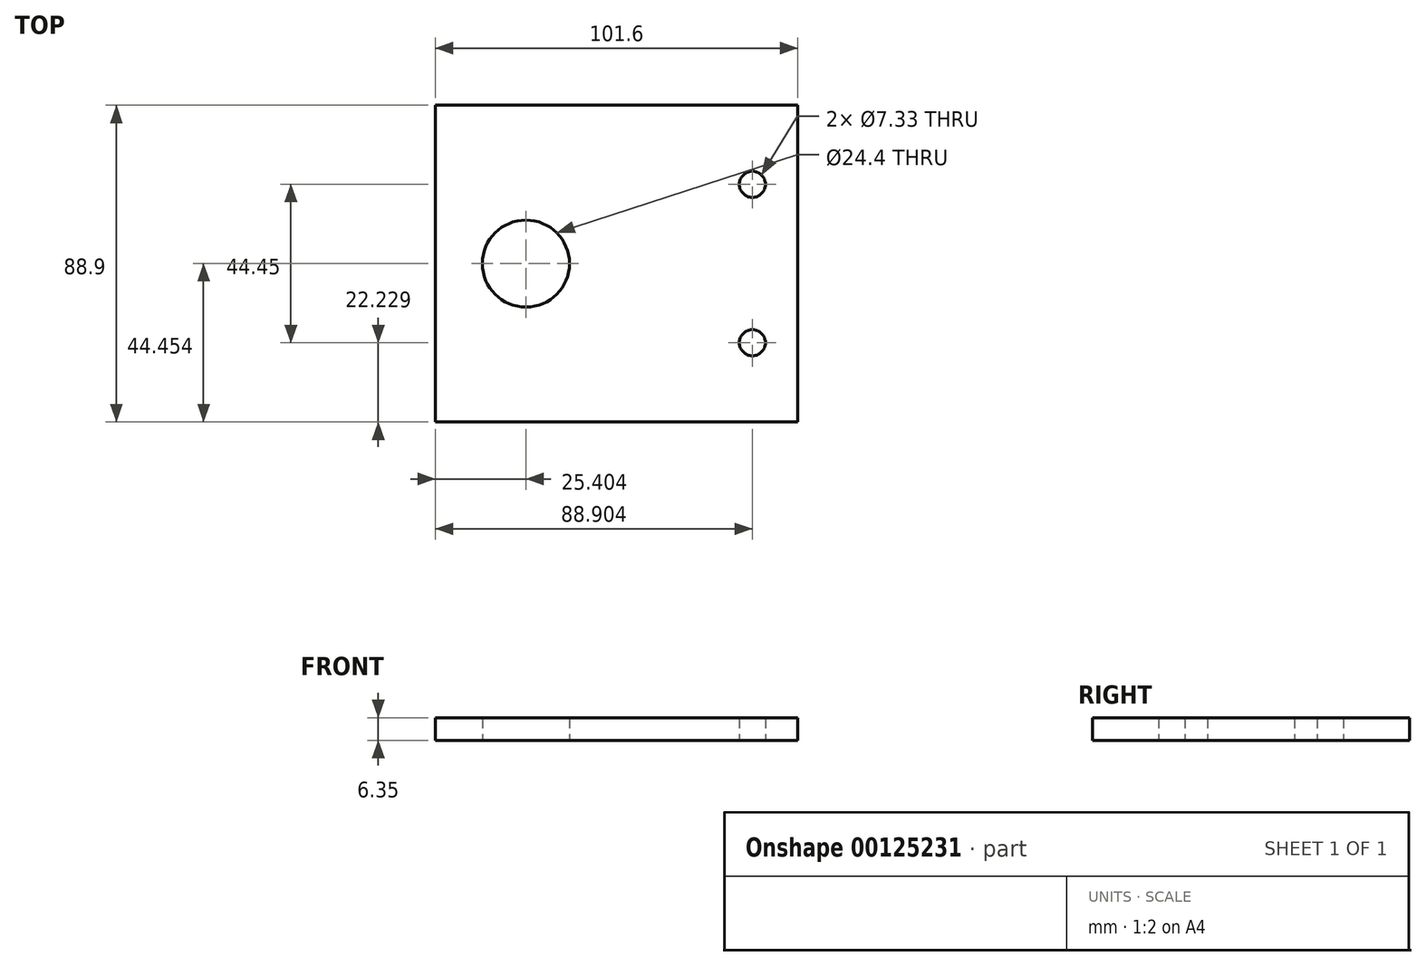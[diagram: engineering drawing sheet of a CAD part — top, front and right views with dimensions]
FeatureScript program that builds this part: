
annotation { "Feature Type Name" : "Feature", "Feature Type Description" : "" }
export const myFeature = defineFeature(function(context is Context, id is Id, definition is map)
    precondition{}
    {
        {
            var Q0;
            Q0=qCreatedBy(makeId("Top.planeOp"),FACE);
            var sketch = newSketch(context, id + "F0", { "sketchPlane" : qUnion([Q0])});
            skLineSegment(sketch, "E0.bottom", {"start": v(-45.86, 38.73) * mm, "end": v(55.74, 38.73) * mm});
            skLineSegment(sketch, "E0.top", {"start": v(-45.86, -50.17) * mm, "end": v(55.74, -50.17) * mm});
            skLineSegment(sketch, "E0.left", {"start": v(-45.86, 38.73) * mm, "end": v(-45.86, -50.17) * mm});
            skLineSegment(sketch, "E0.right", {"start": v(55.74, 38.73) * mm, "end": v(55.74, -50.17) * mm});
            skLineSegment(sketch, "E1", {"start": v(55.74, -50.17) * mm, "end": v(55.74, -5.72) * mm});
            skLineSegment(sketch, "E2", {"start": v(4.94, 38.73) * mm, "end": v(-45.86, 38.73) * mm});
            skCircle(sketch, "E3", {"center": v(-20.46, -5.72) * mm, "radius": 12.2 * mm});
            skLineSegment(sketch, "E4", {"start": v(4.94, -50.17) * mm, "end": v(55.74, -50.17) * mm});
            skLineSegment(sketch, "E5", {"start": v(30.34, -50.17) * mm, "end": v(55.74, -50.17) * mm});
            skLineSegment(sketch, "E6", {"start": v(55.74, 38.73) * mm, "end": v(30.34, 38.73) * mm});
            skLineSegment(sketch, "E7", {"start": v(55.74, 38.73) * mm, "end": v(55.74, -5.72) * mm});
            skPoint(sketch, "E8.endSnap0", {"position": v(43.04, 16.5) * mm});
            skCircle(sketch, "E9", {"center": v(43.04, -27.94) * mm, "radius": 3.66 * mm});
            skCircle(sketch, "E10.MirrorC", {"center": v(43.04, 16.5) * mm, "radius": 3.66 * mm});
            skSolve(sketch);
        }
        {
            var Q0;
            {var subQ0=sQuery(id+"F0.wireOp",EDGE,"E5");var subQ1=sQuery(id+"F0.wireOp",EDGE,"E1");var subQ2=makeQuery(id+"F0.imprint","INTERSECT",VERTEX,{"derivedFrom":[subQ1,subQ0]});Q0=makeQuery(id+"F0.imprint","IMPRINT",FACE,{"disambiguationData":[TD([[makeQuery(id+"F0.imprint","IMPRINT",EDGE,{"disambiguationData":[TD([[subQ2,-1.0]])],"derivedFrom":subQ1}),1.0]])]});}
            var Q1;
            {var subQ0=sQuery(id+"F0.wireOp",EDGE,"LGnLN9mM-Xkxr-LYmd-yJFd-eMDi61Mrex6Q");Q1=makeQuery(id+"F0.imprint","IMPRINT",FACE,{"disambiguationData":[TD([[makeQuery(id+"F0.imprint","IMPRINT",EDGE,{"derivedFrom":subQ0}),-1.0]])]});}
            var Q2;
            {var subQ0=sQuery(id+"F0.wireOp",EDGE,"4gkEirLz-PVHt-gxZv-wHuL-uA4zsXtf7ZB7");var subQ3=sQuery(id+"F0.wireOp",EDGE,"E9");var subQ4=makeQuery(id+"F0.imprint","INTERSECT",VERTEX,{"disambiguationData":[OD(1.0)],"derivedFrom":[subQ0,subQ3]});Q2=makeQuery(id+"F0.imprint","IMPRINT",FACE,{"disambiguationData":[TD([[makeQuery(id+"F0.imprint","IMPRINT",EDGE,{"disambiguationData":[TD([[subQ4,-1.0]])],"derivedFrom":subQ3}),-1.0]])]});}
            var Q3;
            {var subQ5=sQuery(id+"F0.wireOp",EDGE,"4gkEirLz-PVHt-gxZv-wHuL-uA4zsXtf7ZB7");var subQ6=sQuery(id+"F0.wireOp",EDGE,"E5");var subQ7=makeQuery(id+"F0.imprint","INTERSECT",VERTEX,{"derivedFrom":[subQ6,subQ5]});Q3=makeQuery(id+"F0.imprint","IMPRINT",FACE,{"disambiguationData":[TD([[makeQuery(id+"F0.imprint","IMPRINT",EDGE,{"disambiguationData":[TD([[subQ7,-1.0]])],"derivedFrom":subQ5}),1.0]])]});}
            var Q4;
            {var subQ0=sQuery(id+"F0.wireOp",EDGE,"5prSmQyU-TzK9-HcOZ-vm7i-UOhpgT4TSbop");var subQ1=sQuery(id+"F0.wireOp",EDGE,"Egr1iIUk-IRK5-7FaS-Bvml-0EscJEXUckNL");var subQ2=makeQuery(id+"F0.imprint","INTERSECT",VERTEX,{"derivedFrom":[subQ1,subQ0]});Q4=makeQuery(id+"F0.imprint","IMPRINT",FACE,{"disambiguationData":[TD([[makeQuery(id+"F0.imprint","IMPRINT",EDGE,{"disambiguationData":[TD([[subQ2,1.0]])],"derivedFrom":subQ1}),-1.0]])]});}
            var Q5;
            {var subQ0=sQuery(id+"F0.wireOp",EDGE,"5prSmQyU-TzK9-HcOZ-vm7i-UOhpgT4TSbop");var subQ1=sQuery(id+"F0.wireOp",EDGE,"Egr1iIUk-IRK5-7FaS-Bvml-0EscJEXUckNL");var subQ2=makeQuery(id+"F0.imprint","INTERSECT",VERTEX,{"derivedFrom":[subQ1,subQ0]});Q5=makeQuery(id+"F0.imprint","IMPRINT",FACE,{"disambiguationData":[TD([[makeQuery(id+"F0.imprint","IMPRINT",EDGE,{"disambiguationData":[TD([[subQ2,-1.0]])],"derivedFrom":subQ1}),-1.0]])]});}
            var Q6;
            {var subQ0=sQuery(id+"F0.wireOp",EDGE,"Mijz9JX0-2sH6-8IKi-sfOY-e99JbsvFe3Rk");var subQ1=sQuery(id+"F0.wireOp",EDGE,"Egr1iIUk-IRK5-7FaS-Bvml-0EscJEXUckNL");var subQ2=makeQuery(id+"F0.imprint","INTERSECT",VERTEX,{"disambiguationData":[OD(1.0)],"derivedFrom":[subQ1,subQ0]});Q6=makeQuery(id+"F0.imprint","IMPRINT",FACE,{"disambiguationData":[TD([[makeQuery(id+"F0.imprint","IMPRINT",EDGE,{"disambiguationData":[TD([[subQ2,1.0]])],"derivedFrom":subQ0}),-1.0]])]});}
            var Q7;
            {var subQ0=sQuery(id+"F0.wireOp",EDGE,"E4");Q7=makeQuery(id+"F0.imprint","IMPRINT",FACE,{"disambiguationData":[TD([[makeQuery(id+"F0.imprint","IMPRINT",EDGE,{"derivedFrom":subQ0}),1.0]])]});}
            var Q8;
            {var subQ6=sQuery(id+"F0.wireOp",EDGE,"E0.bottom");Q8=makeQuery(id+"F0.imprint","IMPRINT",FACE,{"disambiguationData":[TD([[makeQuery(id+"F0.imprint","IMPRINT",EDGE,{"derivedFrom":subQ6}),-1.0]])]});}
            var Q9;
            {var subQ6=sQuery(id+"F0.wireOp",EDGE,"E0.top");Q9=makeQuery(id+"F0.imprint","IMPRINT",FACE,{"disambiguationData":[TD([[makeQuery(id+"F0.imprint","IMPRINT",EDGE,{"derivedFrom":subQ6}),1.0]])]});}
            var Q10;
            {var subQ0=sQuery(id+"F0.wireOp",EDGE,"Egr1iIUk-IRK5-7FaS-Bvml-0EscJEXUckNL");var subQ1=makeQuery(id+"F0.imprint","INTERSECT",VERTEX,{"derivedFrom":[subQ0,sQuery(id+"F0.wireOp",EDGE,"5prSmQyU-TzK9-HcOZ-vm7i-UOhpgT4TSbop")]});Q10=makeQuery(id+"F0.imprint","IMPRINT",FACE,{"disambiguationData":[TD([[makeQuery(id+"F0.imprint","IMPRINT",EDGE,{"disambiguationData":[TD([[subQ1,1.0]])],"derivedFrom":subQ0}),1.0]])]});}
            var Q11;
            {var subQ0=sQuery(id+"F0.wireOp",EDGE,"DbKO9b2h-4PZE-6dI3-qVEK-g0qfQGCErkgG");var subQ1=sQuery(id+"F0.wireOp",EDGE,"E2");var subQ2=makeQuery(id+"F0.imprint","INTERSECT",VERTEX,{"derivedFrom":[subQ1,subQ0]});Q11=makeQuery(id+"F0.imprint","IMPRINT",FACE,{"disambiguationData":[TD([[makeQuery(id+"F0.imprint","IMPRINT",EDGE,{"disambiguationData":[TD([[subQ2,1.0]])],"derivedFrom":subQ0}),-1.0]])]});}
            var Q12;
            {var subQ1=sQuery(id+"F0.wireOp",EDGE,"E2");var subQ6=sQuery(id+"F0.wireOp",EDGE,"E0.left");var subQ9=makeQuery(id+"F0.imprint","INTERSECT",VERTEX,{"derivedFrom":[subQ6,subQ1]});Q12=makeQuery(id+"F0.imprint","IMPRINT",FACE,{"disambiguationData":[TD([[makeQuery(id+"F0.imprint","IMPRINT",EDGE,{"disambiguationData":[TD([[subQ9,-1.0]])],"derivedFrom":subQ6}),1.0]])]});}
            var Q13;
            {var subQ0=sQuery(id+"F0.wireOp",EDGE,"4gSdTB7D-AjG4-GToR-hZTK-NdP5ZwUg0jW9");var subQ1=sQuery(id+"F0.wireOp",EDGE,"E6");var subQ2=makeQuery(id+"F0.imprint","INTERSECT",VERTEX,{"derivedFrom":[subQ1,subQ0]});Q13=makeQuery(id+"F0.imprint","IMPRINT",FACE,{"disambiguationData":[TD([[makeQuery(id+"F0.imprint","IMPRINT",EDGE,{"disambiguationData":[TD([[subQ2,-1.0]])],"derivedFrom":subQ0}),-1.0]])]});}
            var Q14;
            {var subQ5=sQuery(id+"F0.wireOp",EDGE,"hpycoGpq-fxAt-P2Oc-6dl9-dlmeizIUyImY");var subQ6=sQuery(id+"F0.wireOp",EDGE,"4nKKqHX2-xPNk-PeId-ulya-zJjAF2TvG2JE");var subQ7=makeQuery(id+"F0.imprint","INTERSECT",VERTEX,{"derivedFrom":[subQ6,subQ5]});Q14=makeQuery(id+"F0.imprint","IMPRINT",FACE,{"disambiguationData":[TD([[makeQuery(id+"F0.imprint","IMPRINT",EDGE,{"disambiguationData":[TD([[subQ7,-1.0]])],"derivedFrom":subQ6}),1.0]])]});}
            var Q15;
            {var subQ5=sQuery(id+"F0.wireOp",EDGE,"LGnLN9mM-Xkxr-LYmd-yJFd-eMDi61Mrex6Q");Q15=makeQuery(id+"F0.imprint","IMPRINT",FACE,{"disambiguationData":[TD([[makeQuery(id+"F0.imprint","IMPRINT",EDGE,{"derivedFrom":subQ5}),1.0]])]});}
            var Q16;
            {var subQ1=sQuery(id+"F0.wireOp",EDGE,"E7");var subQ5=sQuery(id+"F0.wireOp",EDGE,"E6");var subQ6=makeQuery(id+"F0.imprint","INTERSECT",VERTEX,{"derivedFrom":[subQ5,subQ1]});Q16=makeQuery(id+"F0.imprint","IMPRINT",FACE,{"disambiguationData":[TD([[makeQuery(id+"F0.imprint","IMPRINT",EDGE,{"disambiguationData":[TD([[subQ6,-1.0]])],"derivedFrom":subQ5}),1.0]])]});}
            extrude(context, id + "F1", {"entities" : qUnion([Q0, Q1, Q2, Q3, Q4, Q5, Q6, Q7, Q8, Q9, Q10, Q11, Q12, Q13, Q14, Q15, Q16]), "depth" : 6.35 * mm});
        }
    });
